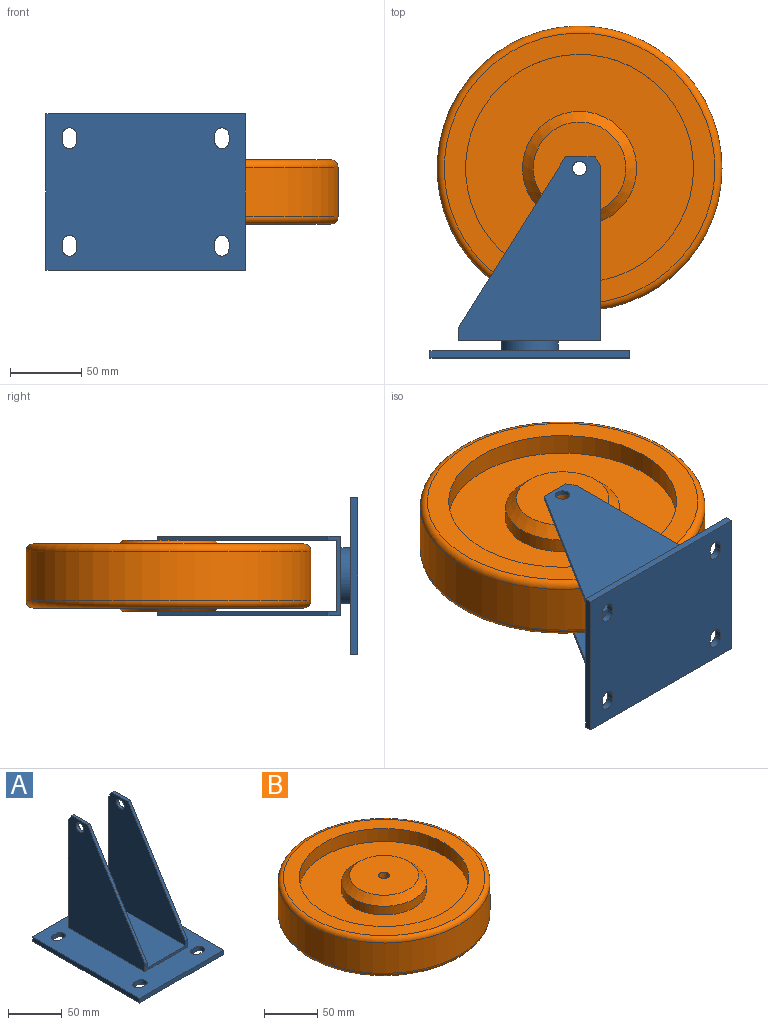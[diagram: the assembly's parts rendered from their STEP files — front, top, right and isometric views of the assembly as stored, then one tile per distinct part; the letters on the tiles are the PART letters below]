
ASSEMBLY  parts=2 mates=1
PART A: 39 faces, bbox 110x140x141 mm
  f0: plane 100x50mm, normal (0,0,1), area 5000mm2, adj f25,f27,f29,f31
  f1: cylinder r=5mm len=10mm, axis (0,0,-1), area 78.6mm2, adj f2,f20,f21,f22
  f2: plane 5x4.47mm, normal (0,1,0), area 22.4mm2, adj f1,f3,f21,f22
  f3: cylinder r=5mm len=10mm, axis (0,0,-1), area 79.8mm2, adj f2,f20,f21,f22
  f4: cylinder r=5mm len=10mm, axis (0,0,-1), area 79.8mm2, adj f5,f16,f21,f22
  f5: plane 5x4.27mm, normal (0,1,0), area 21.3mm2, adj f4,f6,f21,f22
  f6: cylinder r=5mm len=10mm, axis (0,0,-1), area 78.6mm2, adj f5,f16,f21,f22
  f7: plane 140x5mm, normal (1,0,0), area 700mm2, adj f8,f17,f21,f22
  f8: plane 110x5mm, normal (0,1,0), area 550mm2, adj f7,f9,f21,f22
  f9: plane 140x5mm, normal (-1,0,0), area 700mm2, adj f8,f17,f21,f22
  f10: cylinder r=5mm len=10mm, axis (0,0,-1), area 79.8mm2, adj f11,f18,f21,f22
  f11: plane 5x4.47mm, normal (0,-1,0), area 22.4mm2, adj f10,f12,f21,f22
  f12: cylinder r=5mm len=10mm, axis (0,0,-1), area 78.6mm2, adj f11,f18,f21,f22
  f13: cylinder r=5mm len=10mm, axis (0,0,-1), area 79.8mm2, adj f14,f19,f21,f22
  f14: plane 5x4.47mm, normal (0,1,0), area 22.4mm2, adj f13,f15,f21,f22
  f15: cylinder r=5mm len=10mm, axis (0,0,-1), area 78.6mm2, adj f14,f19,f21,f22
  f16: plane 5x4.47mm, normal (0,-1,0), area 22.4mm2, adj f4,f6,f21,f22
  f17: plane 110x5mm, normal (0,-1,0), area 550mm2, adj f7,f9,f21,f22
  f18: plane 5x4.27mm, normal (0,1,0), area 21.3mm2, adj f10,f12,f21,f22
  f19: plane 5x4.27mm, normal (0,-1,0), area 21.3mm2, adj f13,f15,f21,f22
  f20: plane 5x4.27mm, normal (0,-1,0), area 21.3mm2, adj f1,f3,f21,f22
  f21: plane 140x110mm, normal (0,0,1), area 13649.3mm2, adj f1,f2,f3,f4,f5,f6,f7,f8
  f22: plane 140x110mm, normal (0,0,-1), area 14905.9mm2, adj f1,f2,f3,f4,f5,f6,f7,f8
  f23: cylinder r=20mm len=40mm, axis (0,0,-1), area 879.6mm2, adj f21,f28
  f24: plane 129x100mm, normal (1,0,0), area 8308.5mm2, adj f25,f27,f28,f32,f34,f36,f37
  f25: plane 122.5x56mm, normal (0,1,0), area 885mm2, adj f0,f24,f26,f28,f29,f31,f35,f36
  f26: plane 129x100mm, normal (-1,0,0), area 8308.5mm2, adj f25,f27,f28,f30,f33,f35,f38
  f27: plane 56x9mm, normal (0,-1,0), area 204mm2, adj f0,f24,f26,f28,f29,f31,f33,f34
  f28: plane 100x56mm, normal (0,0,-1), area 4343.4mm2, adj f23,f24,f25,f26,f27
  f29: plane 126x100mm, normal (1,0,0), area 8008.5mm2, adj f0,f25,f27,f30,f33,f35,f38
  f30: plane 21x3mm, normal (0,0,1), area 63mm2, adj f26,f29,f33,f35
  f31: plane 126x100mm, normal (-1,0,0), area 8008.5mm2, adj f0,f25,f27,f32,f34,f36,f37
  f32: plane 21x3mm, normal (0,0,1), area 63mm2, adj f24,f31,f34,f36
  f33: plane 120x75mm, normal (0,-0.85,0.53), area 424.5mm2, adj f26,f27,f29,f30
  f34: plane 120x75mm, normal (0,-0.85,0.53), area 424.5mm2, adj f24,f27,f31,f32
  f35: plane 6.5x4mm, normal (0,0.85,0.52), area 22.9mm2, adj f25,f26,f29,f30
  f36: plane 6.5x4mm, normal (0,0.85,0.52), area 22.9mm2, adj f24,f25,f31,f32
  f37: cylinder r=5mm len=10mm, axis (-1,0,0), area 94.2mm2, adj f24,f31
  f38: cylinder r=5mm len=10mm, axis (-1,0,0), area 94.2mm2, adj f26,f29
PART B: 16 faces, bbox 216.5x216.5x50 mm
  f0: cylinder r=40mm len=80mm, axis (0,0,-1), area 2513.3mm2, adj f6,f14
  f1: cylinder r=5mm len=50mm, axis (0,0,-1), area 1570.8mm2, adj f3,f4
  f2: cylinder r=40mm len=80mm, axis (0,0,-1), area 2513.3mm2, adj f5,f15
  f3: plane 65x65mm, normal (0,0,1), area 3239.8mm2, adj f1,f15
  f4: plane 65x65mm, normal (0,0,-1), area 3239.8mm2, adj f1,f14
  f5: plane 160x160mm, normal (0,0,1), area 15079.6mm2, adj f2,f8
  f6: plane 160x160mm, normal (0,0,-1), area 15079.6mm2, adj f0,f7
  f7: cylinder r=80mm len=160mm, axis (0,0,-1), area 7539.8mm2, adj f6,f11
  f8: cylinder r=80mm len=160mm, axis (0,0,-1), area 7539.8mm2, adj f5,f10
  f9: cylinder r=100mm len=200mm, axis (0,0,-1), area 21991.1mm2, adj f12,f13
  f10: plane 190x190mm, normal (0,0,1), area 8246.7mm2, adj f8,f13
  f11: plane 190x190mm, normal (0,0,-1), area 8246.7mm2, adj f7,f12
  f12: torus R=95mm, axis (0,0,1), area 4845.1mm2, adj f9,f11
  f13: torus R=95mm, axis (0,0,1), area 4845.1mm2, adj f9,f10
  f14: cone r=40mm half-angle=45deg, axis (0,0,1), area 2415.8mm2, adj f0,f4
  f15: cone r=32.5mm half-angle=45deg, axis (0,0,-1), area 2415.8mm2, adj f2,f3
PLACE A rot(axis=(-0.58,-0.58,-0.58),120deg) t=(12.57,-117.51,-17.96)mm
PLACE B t=(47.57,15.49,-17.96)mm
MATE revolute A.f37 <-> B.f1  axis (0,0,-1) through (47.57,15.49,7.04)mm
